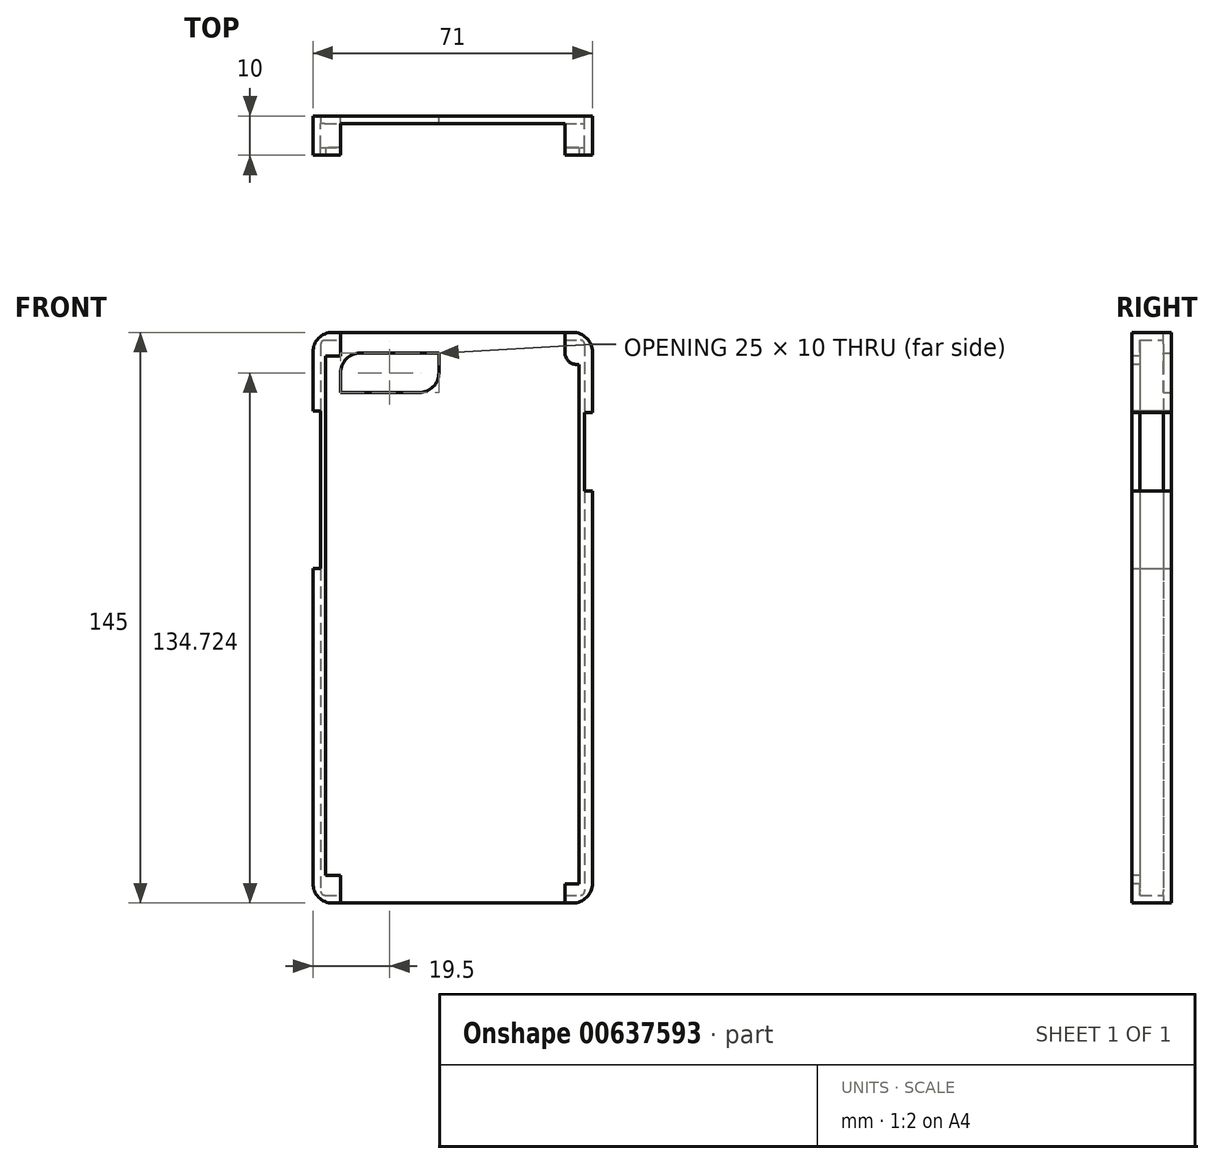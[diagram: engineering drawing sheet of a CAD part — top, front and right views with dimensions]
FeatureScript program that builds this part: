
annotation { "Feature Type Name" : "Feature", "Feature Type Description" : "" }
export const myFeature = defineFeature(function(context is Context, id is Id, definition is map)
    precondition{}
    {
        {
            var Q0;
            Q0=qCreatedBy(makeId("Front.planeOp"),FACE);
            var sketch = newSketch(context, id + "F0", { "sketchPlane" : qUnion([Q0])});
            skLineSegment(sketch, "E0.bottom", {"start": v(-35.5, 72.5) * mm, "end": v(35.5, 72.5) * mm});
            skLineSegment(sketch, "E0.top", {"start": v(-35.5, -72.5) * mm, "end": v(35.5, -72.5) * mm});
            skLineSegment(sketch, "E0.left", {"start": v(-35.5, 72.5) * mm, "end": v(-35.5, -72.5) * mm});
            skLineSegment(sketch, "E0.right", {"start": v(35.5, 72.5) * mm, "end": v(35.5, -72.5) * mm});
            skPoint(sketch, "E0.middle", {"position": v(0, 0) * mm});
            skSolve(sketch);
        }
        {
            var Q0;
            Q0=makeQuery(id+"F0.imprint","IMPRINT",FACE,{"disambiguationData":[TD([[makeQuery(id+"F0.imprint","IMPRINT",EDGE,{"derivedFrom":sQuery(id+"F0.wireOp",EDGE,"E0.bottom")}),-1.0]])]});
            var Q1;
            Q1 = qSketchRegion(id + "F2", true);
            extrude(context, id + "F1", {"entities" : qUnion([Q0, Q1]), "depth" : 2 * mm, "offsetDistance" : 25 * mm});
        }
        {
            var Q0;
            Q0=makeQuery(id+"F1.opExtrude","CAP_FACE",FACE,{"disambiguationData":[OSD([sQuery(id+"F0.wireOp",EDGE,"E0.bottom"),sQuery(id+"F0.wireOp",EDGE,"E0.top"),sQuery(id+"F0.wireOp",EDGE,"E0.left"),sQuery(id+"F0.wireOp",EDGE,"E0.right")])],"isStart":false});
            var sketch = newSketch(context, id + "F2", { "sketchPlane" : qUnion([Q0])});
            skLineSegment(sketch, "E1.bottom", {"start": v(-35.5, 72.5) * mm, "end": v(-28.5, 72.5) * mm});
            skLineSegment(sketch, "E1.top", {"start": v(-35.5, -72.5) * mm, "end": v(-28.5, -72.5) * mm});
            skLineSegment(sketch, "E1.left", {"start": v(-35.5, 72.5) * mm, "end": v(-35.5, -72.5) * mm});
            skLineSegment(sketch, "E1.right", {"start": v(-28.5, 72.5) * mm, "end": v(-28.5, -72.5) * mm});
            skLineSegment(sketch, "E2.bottom", {"start": v(35.5, -72.5) * mm, "end": v(28.5, -72.5) * mm});
            skLineSegment(sketch, "E2.top", {"start": v(35.5, 72.5) * mm, "end": v(28.5, 72.5) * mm});
            skLineSegment(sketch, "E2.left", {"start": v(35.5, -72.5) * mm, "end": v(35.5, 72.5) * mm});
            skLineSegment(sketch, "E2.right", {"start": v(28.5, -72.5) * mm, "end": v(28.5, 72.5) * mm});
            skSolve(sketch);
        }
        {
            var Q0;
            Q0=makeQuery(id+"F2.imprint","IMPRINT",FACE,{"disambiguationData":[TD([[makeQuery(id+"F2.imprint","IMPRINT",EDGE,{"derivedFrom":sQuery(id+"F2.wireOp",EDGE,"E1.bottom")}),-1.0]])]});
            var Q1;
            Q1=makeQuery(id+"F2.imprint","IMPRINT",FACE,{"disambiguationData":[TD([[makeQuery(id+"F2.imprint","IMPRINT",EDGE,{"derivedFrom":sQuery(id+"F2.wireOp",EDGE,"E2.bottom")}),1.0]])]});
            extrude(context, id + "F3", {"entities" : qUnion([Q0, Q1]), "operationType" : NewBodyOperationType.ADD, "depth" : 8 * mm, "offsetDistance" : 25 * mm});
        }
        {
            var Q0;
            Q0=makeQuery(id+"F3.opExtrude","SWEPT_FACE",FACE,{"disambiguationData":[OSD([sQuery(id+"F2.wireOp",EDGE,"E1.right")])]});
            var Q1;
            Q1=makeQuery(id+"F3.opExtrude","SWEPT_FACE",FACE,{"disambiguationData":[OSD([sQuery(id+"F2.wireOp",EDGE,"E2.right")])]});
            shell(context, id + "F4", {"entities" : qUnion([Q0, Q1]), "thickness" : 2 * mm});
        }
        {
            var Q0;
            Q0=makeQuery(id+"F3.opExtrude","CAP_FACE",FACE,{"disambiguationData":[OSD([sQuery(id+"F2.wireOp",EDGE,"E1.bottom"),sQuery(id+"F2.wireOp",EDGE,"E1.top"),sQuery(id+"F2.wireOp",EDGE,"E1.left"),sQuery(id+"F2.wireOp",EDGE,"E1.right")])],"isStart":false});
            var sketch = newSketch(context, id + "F5", { "sketchPlane" : qUnion([Q0])});
            skLineSegment(sketch, "E3", {"start": v(-28.5, 66.48) * mm, "end": v(-32.25, 66.48) * mm});
            skLineSegment(sketch, "E4", {"start": v(-32.25, 66.48) * mm, "end": v(-32.25, -65.46) * mm});
            skLineSegment(sketch, "E5", {"start": v(-32.25, -65.46) * mm, "end": v(-28.5, -65.46) * mm});
            skLineSegment(sketch, "E6", {"start": v(-28.5, -65.46) * mm, "end": v(-28.5, 66.48) * mm});
            skSolve(sketch);
        }
        {
            var Q0;
            Q0=makeQuery(id+"F5.imprint","IMPRINT",FACE,{"disambiguationData":[TD([[makeQuery(id+"F5.imprint","IMPRINT",EDGE,{"derivedFrom":sQuery(id+"F5.wireOp",EDGE,"E3")}),1.0]])]});
            extrude(context, id + "F6", {"entities" : qUnion([Q0]), "operationType" : NewBodyOperationType.REMOVE, "oppositeDirection" : true, "depth" : 2 * mm, "offsetDistance" : 25 * mm});
        }
        {
            var Q0;
            Q0=makeQuery(id+"F3.opExtrude","CAP_FACE",FACE,{"disambiguationData":[OSD([sQuery(id+"F2.wireOp",EDGE,"E2.bottom"),sQuery(id+"F2.wireOp",EDGE,"E2.top"),sQuery(id+"F2.wireOp",EDGE,"E2.left"),sQuery(id+"F2.wireOp",EDGE,"E2.right")])],"isStart":false});
            var sketch = newSketch(context, id + "F7", { "sketchPlane" : qUnion([Q0])});
            skLineSegment(sketch, "E7", {"start": v(28.5, 64.34) * mm, "end": v(32.05, 64.34) * mm});
            skLineSegment(sketch, "E8", {"start": v(32.05, 64.34) * mm, "end": v(32.05, -67.6) * mm});
            skLineSegment(sketch, "E9", {"start": v(32.05, -67.6) * mm, "end": v(28.5, -67.6) * mm});
            skLineSegment(sketch, "E10", {"start": v(28.5, -67.6) * mm, "end": v(28.5, 64.34) * mm});
            skSolve(sketch);
        }
        {
            var Q0;
            Q0=makeQuery(id+"F7.imprint","IMPRINT",FACE,{"disambiguationData":[TD([[makeQuery(id+"F7.imprint","IMPRINT",EDGE,{"derivedFrom":sQuery(id+"F7.wireOp",EDGE,"E7")}),-1.0]])]});
            extrude(context, id + "F8", {"entities" : qUnion([Q0]), "operationType" : NewBodyOperationType.REMOVE, "oppositeDirection" : true, "depth" : 2 * mm, "offsetDistance" : 25 * mm});
        }
        {
            var Q0;
            Q0=makeQuery(id+"F3.boolean.opBoolean","MERGE",EDGE,{"derivedFrom":[makeQuery(id+"F1.opExtrude","SWEPT_EDGE",EDGE,{"disambiguationData":[OSD([sQuery(id+"F0.wireOp",EDGE,"E0.bottom"),sQuery(id+"F0.wireOp",EDGE,"E0.left")])]}),makeQuery(id+"F3.opExtrude","SWEPT_EDGE",EDGE,{"disambiguationData":[OSD([sQuery(id+"F2.wireOp",EDGE,"E1.bottom"),sQuery(id+"F2.wireOp",EDGE,"E1.left")])]})]});
            var Q1;
            Q1=makeQuery(id+"F3.boolean.opBoolean","MERGE",EDGE,{"derivedFrom":[makeQuery(id+"F1.opExtrude","SWEPT_EDGE",EDGE,{"disambiguationData":[OSD([sQuery(id+"F0.wireOp",EDGE,"E0.bottom"),sQuery(id+"F0.wireOp",EDGE,"E0.right")])]}),makeQuery(id+"F3.opExtrude","SWEPT_EDGE",EDGE,{"disambiguationData":[OSD([sQuery(id+"F2.wireOp",EDGE,"E2.top"),sQuery(id+"F2.wireOp",EDGE,"E2.left")])]})]});
            var Q2;
            Q2=makeQuery(id+"F3.boolean.opBoolean","MERGE",EDGE,{"derivedFrom":[makeQuery(id+"F1.opExtrude","SWEPT_EDGE",EDGE,{"disambiguationData":[OSD([sQuery(id+"F0.wireOp",EDGE,"E0.top"),sQuery(id+"F0.wireOp",EDGE,"E0.right")])]}),makeQuery(id+"F3.opExtrude","SWEPT_EDGE",EDGE,{"disambiguationData":[OSD([sQuery(id+"F2.wireOp",EDGE,"E2.bottom"),sQuery(id+"F2.wireOp",EDGE,"E2.left")])]})]});
            var Q3;
            Q3=makeQuery(id+"F3.boolean.opBoolean","MERGE",EDGE,{"derivedFrom":[makeQuery(id+"F1.opExtrude","SWEPT_EDGE",EDGE,{"disambiguationData":[OSD([sQuery(id+"F0.wireOp",EDGE,"E0.top"),sQuery(id+"F0.wireOp",EDGE,"E0.left")])]}),makeQuery(id+"F3.opExtrude","SWEPT_EDGE",EDGE,{"disambiguationData":[OSD([sQuery(id+"F2.wireOp",EDGE,"E1.top"),sQuery(id+"F2.wireOp",EDGE,"E1.left")])]})]});
            fillet(context, id + "F9", {"entities" : qUnion([Q0, Q1, Q2, Q3]), "radius" : 5 * mm, "tangentPropagation" : true, "allowEdgeOverflow" : false});
        }
        {
            var Q0;
            Q0=makeQuery(id+"F1.opExtrude","CAP_FACE",FACE,{"disambiguationData":[OSD([sQuery(id+"F0.wireOp",EDGE,"E0.bottom"),sQuery(id+"F0.wireOp",EDGE,"E0.top"),sQuery(id+"F0.wireOp",EDGE,"E0.left"),sQuery(id+"F0.wireOp",EDGE,"E0.right")])],"isStart":true});
            var sketch = newSketch(context, id + "F10", { "sketchPlane" : qUnion([Q0])});
            skLineSegment(sketch, "E11.bottom", {"start": v(23.5, 67.22) * mm, "end": v(3.5, 67.22) * mm});
            skLineSegment(sketch, "E11.top", {"start": v(28.5, 57.22) * mm, "end": v(8.5, 57.22) * mm});
            skLineSegment(sketch, "E11.left", {"start": v(28.5, 62.22) * mm, "end": v(28.5, 57.22) * mm});
            skLineSegment(sketch, "E11.right", {"start": v(3.5, 67.22) * mm, "end": v(3.5, 62.22) * mm});
            skPoint(sketch, "E12.visualSharp", {"position": v(28.5, 67.22) * mm});
            skArc(sketch, "E12.filletArc", {"start": v(28.5, 62.22) * mm, "mid": v(27.04, 65.76) * mm, "end": v(23.5, 67.22) * mm});
            skPoint(sketch, "E13.visualSharp", {"position": v(3.5, 57.22) * mm});
            skArc(sketch, "E13.filletArc", {"start": v(3.5, 62.22) * mm, "mid": v(4.96, 58.69) * mm, "end": v(8.5, 57.22) * mm});
            skSolve(sketch);
        }
        {
            var Q0;
            Q0 = qSketchRegion(id + "F10", true);
            extrude(context, id + "F11", {"entities" : qUnion([Q0]), "operationType" : NewBodyOperationType.REMOVE, "oppositeDirection" : true, "depth" : 2.5 * mm, "offsetDistance" : 25 * mm});
        }
        {
            var Q0;
            Q0=makeQuery(id+"F3.boolean.opBoolean","MERGE",FACE,{"derivedFrom":[makeQuery(id+"F1.opExtrude","SWEPT_FACE",FACE,{"disambiguationData":[OSD([sQuery(id+"F0.wireOp",EDGE,"E0.left")])]}),makeQuery(id+"F3.opExtrude","SWEPT_FACE",FACE,{"disambiguationData":[OSD([sQuery(id+"F2.wireOp",EDGE,"E1.left")])]})]});
            var sketch = newSketch(context, id + "F12", { "sketchPlane" : qUnion([Q0])});
            skLineSegment(sketch, "E14.bottom", {"start": v(0, 52.5) * mm, "end": v(10, 52.5) * mm});
            skLineSegment(sketch, "E14.top", {"start": v(0, 59.56) * mm, "end": v(10, 59.56) * mm});
            skLineSegment(sketch, "E14.left", {"start": v(0, 52.5) * mm, "end": v(0, 59.56) * mm});
            skLineSegment(sketch, "E14.right", {"start": v(10, 52.5) * mm, "end": v(10, 59.56) * mm});
            skLineSegment(sketch, "E15.bottom", {"start": v(10, 12.5) * mm, "end": v(0, 12.5) * mm});
            skLineSegment(sketch, "E16.left", {"start": v(0, 52.5) * mm, "end": v(0, 52.75) * mm});
            skLineSegment(sketch, "E17.left", {"start": v(10, 12.5) * mm, "end": v(10, 47.07) * mm});
            skLineSegment(sketch, "E17.right", {"start": v(0, 12.5) * mm, "end": v(0, 59.56) * mm});
            skSolve(sketch);
        }
        {
            var Q0;
            {var subQ0=sQuery(id+"F12.wireOp",EDGE,"E14.bottom");Q0=makeQuery(id+"F12.imprint","IMPRINT",FACE,{"disambiguationData":[TD([[makeQuery(id+"F12.imprint","IMPRINT",EDGE,{"derivedFrom":subQ0}),-1.0]])]});}
            extrude(context, id + "F13", {"entities" : qUnion([Q0]), "operationType" : NewBodyOperationType.REMOVE, "oppositeDirection" : true, "depth" : 2 * mm, "offsetDistance" : 25 * mm});
        }
        {
            var Q0;
            Q0=makeQuery(id+"F3.boolean.opBoolean","MERGE",FACE,{"derivedFrom":[makeQuery(id+"F1.opExtrude","SWEPT_FACE",FACE,{"disambiguationData":[OSD([sQuery(id+"F0.wireOp",EDGE,"E0.right")])]}),makeQuery(id+"F3.opExtrude","SWEPT_FACE",FACE,{"disambiguationData":[OSD([sQuery(id+"F2.wireOp",EDGE,"E2.left")])]})]});
            var sketch = newSketch(context, id + "F14", { "sketchPlane" : qUnion([Q0])});
            skLineSegment(sketch, "E18.bottom", {"start": v(-10, 52.13) * mm, "end": v(0, 52.13) * mm});
            skLineSegment(sketch, "E18.top", {"start": v(-10, 32.13) * mm, "end": v(0, 32.13) * mm});
            skLineSegment(sketch, "E18.left", {"start": v(-10, 52.13) * mm, "end": v(-10, 32.13) * mm});
            skLineSegment(sketch, "E18.right", {"start": v(0, 52.13) * mm, "end": v(0, 32.13) * mm});
            skSolve(sketch);
        }
        {
            var Q0;
            Q0=makeQuery(id+"F8.boolean.opBoolean","COPY",EDGE,{"derivedFrom":makeQuery(id+"F8.opExtrude","SWEPT_EDGE",EDGE,{"disambiguationData":[OSD([sQuery(id+"F2.wireOp",EDGE,"E2.right"),sQuery(id+"F7.wireOp",EDGE,"E7"),sQuery(id+"F7.wireOp",EDGE,"E10")])]})});
            var Q1;
            Q1=makeQuery(id+"F6.boolean.opBoolean","COPY",EDGE,{"derivedFrom":makeQuery(id+"F6.opExtrude","SWEPT_EDGE",EDGE,{"disambiguationData":[OSD([sQuery(id+"F2.wireOp",EDGE,"E1.right"),sQuery(id+"F5.wireOp",EDGE,"E3"),sQuery(id+"F5.wireOp",EDGE,"E6")])]})});
            var Q2;
            Q2=makeQuery(id+"F8.boolean.opBoolean","COPY",EDGE,{"derivedFrom":makeQuery(id+"F8.opExtrude","CAP_EDGE",EDGE,{"disambiguationData":[OSD([sQuery(id+"F7.wireOp",EDGE,"E9")])],"isStart":false})});
            var Q3;
            Q3=makeQuery(id+"F6.boolean.opBoolean","COPY",EDGE,{"derivedFrom":makeQuery(id+"F6.opExtrude","CAP_EDGE",EDGE,{"disambiguationData":[OSD([sQuery(id+"F5.wireOp",EDGE,"E5")])],"isStart":false})});
            fillet(context, id + "F15", {"entities" : qUnion([Q0, Q1, Q2, Q3]), "radius" : 3 * mm, "tangentPropagation" : true, "allowEdgeOverflow" : false});
        }
        {
            var Q0;
            Q0=makeQuery(id+"F4.opShell","OFFSET_EDGE",EDGE,{"disambiguationData":[OSD([sQuery(id+"F0.wireOp",EDGE,"E0.bottom"),sQuery(id+"F0.wireOp",EDGE,"E0.right"),sQuery(id+"F2.wireOp",EDGE,"E2.top"),sQuery(id+"F2.wireOp",EDGE,"E2.left")])]});
            var Q1;
            Q1=makeQuery(id+"F4.opShell","OFFSET_EDGE",EDGE,{"disambiguationData":[OSD([sQuery(id+"F0.wireOp",EDGE,"E0.bottom"),sQuery(id+"F0.wireOp",EDGE,"E0.left"),sQuery(id+"F2.wireOp",EDGE,"E1.bottom"),sQuery(id+"F2.wireOp",EDGE,"E1.left")])]});
            var Q2;
            Q2=makeQuery(id+"F4.opShell","OFFSET_EDGE",EDGE,{"disambiguationData":[OSD([sQuery(id+"F0.wireOp",EDGE,"E0.top"),sQuery(id+"F0.wireOp",EDGE,"E0.left"),sQuery(id+"F2.wireOp",EDGE,"E1.top"),sQuery(id+"F2.wireOp",EDGE,"E1.left")])]});
            var Q3;
            Q3=makeQuery(id+"F4.opShell","OFFSET_EDGE",EDGE,{"disambiguationData":[OSD([sQuery(id+"F0.wireOp",EDGE,"E0.top"),sQuery(id+"F0.wireOp",EDGE,"E0.right"),sQuery(id+"F2.wireOp",EDGE,"E2.bottom"),sQuery(id+"F2.wireOp",EDGE,"E2.left")])]});
            fillet(context, id + "F16", {"entities" : qUnion([Q0, Q1, Q2, Q3]), "radius" : 1 * mm, "tangentPropagation" : true, "allowEdgeOverflow" : false});
        }
        {
            var Q0;
            Q0 = qSketchRegion(id + "F14", true);
            extrude(context, id + "F17", {"entities" : qUnion([Q0]), "operationType" : NewBodyOperationType.REMOVE, "oppositeDirection" : true, "depth" : 2 * mm, "offsetDistance" : 25 * mm});
        }
    });
